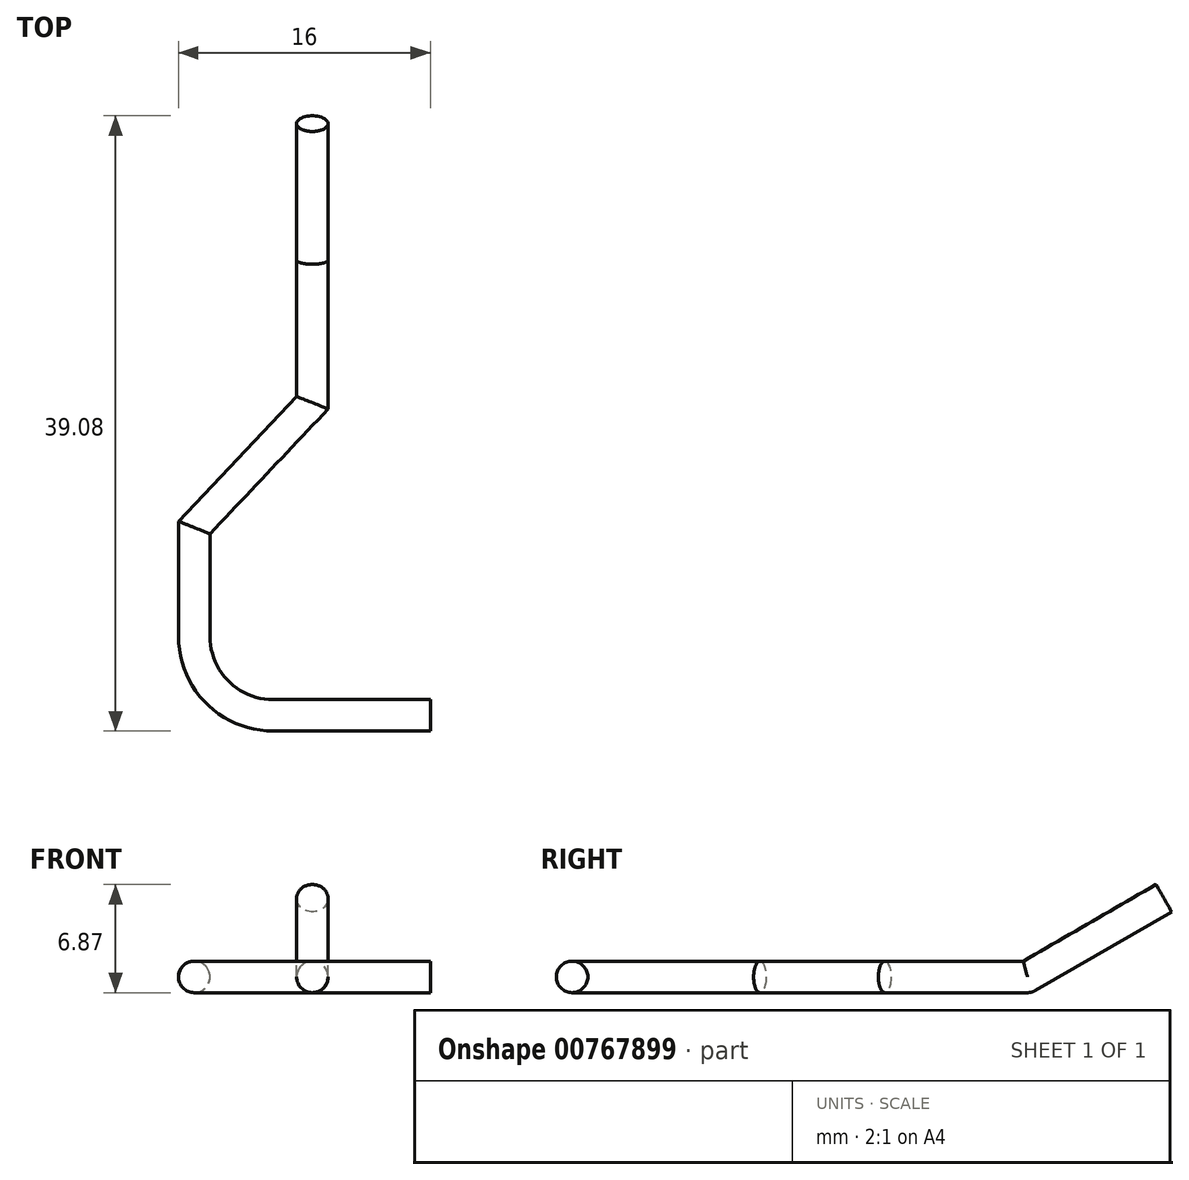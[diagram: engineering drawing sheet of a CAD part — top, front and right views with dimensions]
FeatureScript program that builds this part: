
annotation { "Feature Type Name" : "Feature", "Feature Type Description" : "" }
export const myFeature = defineFeature(function(context is Context, id is Id, definition is map)
    precondition{}
    {
        {
            var Q0;
            Q0=qCreatedBy(makeId("Top.planeOp"),FACE);
            var sketch = newSketch(context, id + "F0", { "sketchPlane" : qUnion([Q0])});
            skLineSegment(sketch, "E0", {"start": v(-7.5, -17) * mm, "end": v(-7.5, -23.92) * mm});
            skLineSegment(sketch, "E1", {"start": v(-2.5, -28.92) * mm, "end": v(7.5, -28.92) * mm});
            skPoint(sketch, "E2.visualSharp", {"position": v(-7.5, -28.92) * mm});
            skArc(sketch, "E2.filletArc", {"start": v(-7.5, -23.92) * mm, "mid": v(-6.04, -27.46) * mm, "end": v(-2.5, -28.92) * mm});
            skLineSegment(sketch, "E3", {"start": v(-7.5, -17) * mm, "end": v(0, -9.07) * mm});
            skLineSegment(sketch, "E4", {"start": v(0, -9.07) * mm, "end": v(0, 0) * mm});
            skSolve(sketch);
        }
        {
            var Q0;
            Q0=qCreatedBy(makeId("Front.planeOp"),FACE);
            var sketch = newSketch(context, id + "F1", { "sketchPlane" : qUnion([Q0])});
            skCircle(sketch, "E5", {"center": v(0, 0) * mm, "radius": 1 * mm});
            skSolve(sketch);
        }
        {
            var Q0;
            Q0 = qSketchRegion(id + "F1", true);
            var Q1;
            Q1 = qConstructionFilter(qBodyType(qCreatedBy(id + "F0" ,EDGE), BodyType.WIRE), ConstructionObject.NO);
            sweep(context, id + "F2", {"profiles" : qUnion([Q0]), "path" : qUnion([Q1])});
        }
        {
            var Q0;
            Q0=makeQuery(id+"F2.opSweep","CAP_FACE",FACE,{"disambiguationData":[OSD([sQuery(id+"F0.wireOp",VERTEX,"E4.end"),sQuery(id+"F1.wireOp",EDGE,"E5")])],"isStart":true});
            var sketch = newSketch(context, id + "F3", { "sketchPlane" : qUnion([Q0])});
            skLineSegment(sketch, "E6", {"start": v(1, 0) * mm, "end": v(-1, 0) * mm});
            skSolve(sketch);
        }
        {
            var Q0;
            Q0=sQuery(id+"F3.wireOp",EDGE,"E6");
            cPlane(context, id + "F4", {"entities" : qUnion([Q0]), "cplaneType" : CPlaneType.LINE_ANGLE, "offset" : 25 * mm, "angle" : 30 * degree, "width" : 150 * mm, "height" : 150 * mm});
        }
        {
            var Q0;
            Q0=qCreatedBy(id+"F4.planeOp",FACE);
            var sketch = newSketch(context, id + "F5", { "sketchPlane" : qUnion([Q0])});
            skCircle(sketch, "E7", {"center": v(0, 0) * mm, "radius": 1 * mm});
            skSolve(sketch);
        }
        {
            var Q0;
            Q0=qCreatedBy(makeId("Top.planeOp"),FACE);
            var sketch = newSketch(context, id + "F6", { "sketchPlane" : qUnion([Q0])});
            skLineSegment(sketch, "E8", {"start": v(0, 0) * mm, "end": v(0, 9.3) * mm});
            skSolve(sketch);
        }
        {
            var Q0;
            Q0=qCreatedBy(makeId("Right.planeOp"),FACE);
            var sketch = newSketch(context, id + "F7", { "sketchPlane" : qUnion([Q0])});
            skLineSegment(sketch, "E9", {"start": v(0, 0) * mm, "end": v(8.66, 5) * mm});
            skSolve(sketch);
        }
        {
            var Q0;
            Q0=makeQuery(id+"F5.imprint","IMPRINT",FACE,{"disambiguationData":[TD([[makeQuery(id+"F5.imprint","IMPRINT",EDGE,{"derivedFrom":sQuery(id+"F5.wireOp",EDGE,"E7")}),1.0]])]});
            var Q1;
            Q1=sQuery(id+"F7.wireOp",EDGE,"E9");
            sweep(context, id + "F8", {"operationType" : NewBodyOperationType.ADD, "profiles" : qUnion([Q0]), "path" : qUnion([Q1])});
        }
        {
            var Q0;
            {var subQ0=sQuery(id+"F3.wireOp",EDGE,"E6");Q0=makeQuery(id+"F3.imprint","IMPRINT",FACE,{"disambiguationData":[TD([[makeQuery(id+"F3.imprint","IMPRINT",EDGE,{"derivedFrom":subQ0}),1.0]])]});}
            var Q1;
            Q1=sQuery(id+"F3.wireOp",EDGE,"E6");
            revolve(context, id + "F9", {"operationType" : NewBodyOperationType.ADD, "surfaceOperationType" : NewSurfaceOperationType.NEW, "entities" : qUnion([Q0]), "axis" : qUnion([Q1]), "revolveType" : RevolveType.ONE_DIRECTION, "angle" : 30 * degree});
        }
    });
